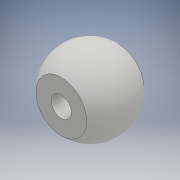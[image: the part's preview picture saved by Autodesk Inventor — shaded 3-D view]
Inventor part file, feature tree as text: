
AUTODESK INVENTOR PART (.ipt)
format: ipt  version: 2017 (Build 210142000, 142)  size: 134,656 bytes
history: native  units: mm
features: sketch x3, extrude x2, revolve x1, plane x1, mirror x1
ambient origin geometry x8: Origin, YZ Plane, XZ Plane, XY Plane, X Axis, Y Axis, Z Axis, Center Point
bodies: Solid1 (feature_tree)
feature tree (8):
  revolve  "Revolution1"  Angle=90.0deg
  extrude  "Extrusion1"  Depth=10.0mm TaperAngle=0.0deg
  plane  "Work Plane1"
  extrude  "Extrusion2"  Depth=12.0mm TaperAngle=0.0deg
  mirror  "Mirror1"
  sketch  "Sketch1"  dims[d0=24.0mm d1=90.0deg]
  sketch  "Sketch2"  dims[d2=6.35mm d3=10.0mm d4=0.0mm]
  sketch  "Sketch3"  dims[d5=12.0mm d6=3.0mm d7=0.0mm]
